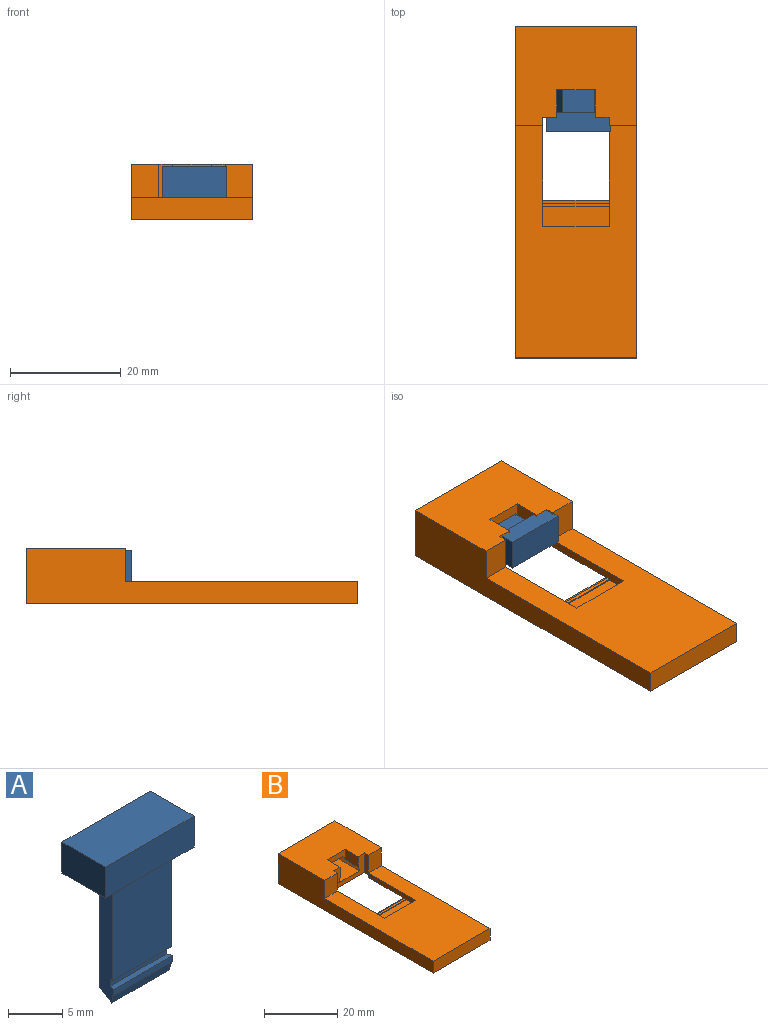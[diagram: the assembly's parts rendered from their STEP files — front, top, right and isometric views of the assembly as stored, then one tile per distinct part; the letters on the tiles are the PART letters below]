
ASSEMBLY  parts=2 mates=1
PART A: 17 faces, bbox 11.6x5.7x17 mm
  f0: plane 13.5x2.8mm, normal (-0.94,0.35,0), area 38.4mm2, adj f2,f3,f4,f5,f6,f7,f8,f9
  f1: plane 13.5x2.8mm, normal (0.94,0.35,0), area 38.4mm2, adj f2,f3,f4,f5,f6,f7,f8,f9
  f2: plane 13.5x5.7mm, normal (0,1,0), area 76.9mm2, adj f0,f1,f4,f9
  f3: plane 10.8x7.7mm, normal (0,-1,0), area 83.2mm2, adj f0,f1,f8,f9
  f4: plane 7.55x2.5mm, normal (0,0,-1), area 16.6mm2, adj f0,f1,f2,f5
  f5: plane 7.7x1mm, normal (0,-0.98,-0.2), area 7.8mm2, adj f0,f1,f4,f16
  f6: plane 7.77x0.6mm, normal (0,0,1), area 4.5mm2, adj f0,f1,f7,f15
  f7: plane 7.33x0.5mm, normal (0,-1,0), area 3.7mm2, adj f0,f1,f6,f8
  f8: cylinder r=0.5mm len=7.7mm, axis (1,0,0), area 5.9mm2, adj f0,f1,f3,f7
  f9: plane 11.6x5.7mm, normal (0,0,-1), area 48mm2, adj f0,f1,f2,f3,f10,f11,f12,f13
  f10: plane 11.6x3.5mm, normal (0,1,0), area 40.6mm2, adj f9,f11,f13,f14
  f11: plane 5.7x3.5mm, normal (-1,0,0), area 19.9mm2, adj f9,f10,f12,f14
  f12: plane 11.6x3.5mm, normal (0,-1,0), area 40.6mm2, adj f9,f11,f13,f14
  f13: plane 5.7x3.5mm, normal (1,0,0), area 19.9mm2, adj f9,f10,f12,f14
  f14: plane 11.6x5.7mm, normal (0,0,1), area 66.1mm2, adj f10,f11,f12,f13
  f15: plane 7.77x0.7mm, normal (0,-1,0), area 5.4mm2, adj f0,f1,f6,f16
  f16: plane 7.77x0.1mm, normal (0,0,-1), area 0.8mm2, adj f0,f1,f5,f15
PART B: 51 faces, bbox 22x60x10 mm
  f0: plane 8x2mm, normal (0,0,1), area 16mm2, adj f3,f43,f44,f48
  f1: plane 22x18mm, normal (0,0,1), area 343mm2, adj f4,f5,f10,f18,f19,f21,f25,f26
  f2: plane 10x6mm, normal (0,0,-1), area 60mm2, adj f3,f43,f44,f47
  f3: plane 15x3mm, normal (0.95,0,-0.32), area 39.5mm2, adj f0,f2,f4,f42,f44,f45,f47,f48
  f4: plane 12x6.5mm, normal (0,-1,0), area 42.2mm2, adj f1,f3,f10,f26,f41,f42,f43,f45
  f5: plane 6x5mm, normal (0,-1,0), area 30mm2, adj f1,f8,f10,f19
  f6: plane 13.5x3.5mm, normal (0,0,-1), area 47.2mm2, adj f10,f11,f15,f39
  f7: plane 13.5x3.5mm, normal (0,0,-1), area 47.2mm2, adj f11,f24,f26,f40
  f8: plane 42x22mm, normal (0,0,1), area 705.6mm2, adj f5,f10,f19,f20,f21,f25,f26,f34
  f9: plane 12x0.5mm, normal (0,0,1), area 6mm2, adj f10,f11,f26,f37
  f10: plane 19.7x7.6mm, normal (1,0,0), area 37.4mm2, adj f1,f4,f5,f6,f8,f9,f11,f34
  f11: plane 19x0.9mm, normal (0,1,0), area 11.6mm2, adj f6,f7,f9,f10,f12,f15,f24,f26
  f12: plane 5.95x5mm, normal (0,0,-1), area 29.7mm2, adj f11,f13,f15,f31
  f13: plane 19x0.9mm, normal (0,-1,0), area 12.8mm2, adj f12,f14,f15,f24,f30,f31,f32,f33
  f14: plane 19x5.2mm, normal (0,0,-1), area 98.8mm2, adj f13,f15,f24,f28
  f15: plane 57x3.5mm, normal (1,0,0), area 154.3mm2, adj f6,f11,f12,f13,f14,f16,f17,f22
  f16: plane 19x16mm, normal (0,0,-1), area 304mm2, adj f15,f22,f24,f27
  f17: plane 60x22mm, normal (0,0,-1), area 237mm2, adj f15,f18,f19,f20,f21,f22,f23,f24
  f18: plane 22x10mm, normal (0,1,0), area 220mm2, adj f1,f17,f19,f21
  f19: plane 60x10mm, normal (-1,0,0), area 348mm2, adj f1,f5,f8,f17,f18,f20
  f20: plane 22x4mm, normal (0,-1,0), area 88mm2, adj f8,f17,f19,f21
  f21: plane 60x10mm, normal (1,0,0), area 348mm2, adj f1,f8,f17,f18,f20,f25
  f22: plane 19x2.5mm, normal (0,1,0), area 47.5mm2, adj f15,f16,f17,f24
  f23: plane 19x3.5mm, normal (0,-1,0), area 66.5mm2, adj f15,f17,f24,f41
  f24: plane 57x3.5mm, normal (-1,0,0), area 154.3mm2, adj f7,f11,f13,f14,f16,f17,f22,f23
  f25: plane 6x5mm, normal (0,-1,0), area 30mm2, adj f1,f8,f21,f26
  f26: plane 19.7x7.6mm, normal (-1,0,0), area 37.4mm2, adj f1,f4,f7,f8,f9,f11,f25,f34
  f27: plane 19x0.3mm, normal (0,-1,0), area 5.7mm2, adj f15,f16,f24,f29
  f28: plane 19x0.3mm, normal (0,1,0), area 5.7mm2, adj f14,f15,f24,f29
  f29: plane 19x0.8mm, normal (0,0,-1), area 15.2mm2, adj f15,f24,f27,f28
  f30: plane 5.95x5mm, normal (0,0,-1), area 29.7mm2, adj f11,f13,f24,f32
  f31: plane 5x0.6mm, normal (1,0,0), area 3mm2, adj f11,f12,f13,f33
  f32: plane 5x0.6mm, normal (-1,0,0), area 3mm2, adj f11,f13,f30,f33
  f33: plane 7.1x5mm, normal (0,0,-1), area 35.5mm2, adj f11,f13,f31,f32
  f34: plane 12x1.6mm, normal (0,1,0), area 19.2mm2, adj f8,f10,f26,f35
  f35: plane 12x3.6mm, normal (0,0,1), area 43.2mm2, adj f10,f26,f34,f36
  f36: plane 12x0.2mm, normal (0,-1,0), area 2.4mm2, adj f10,f26,f35,f38
  f37: plane 12x0.2mm, normal (0,1,0), area 2.4mm2, adj f9,f10,f26,f38
  f38: plane 12x0.6mm, normal (0,0,1), area 7.2mm2, adj f10,f26,f36,f37
  f39: plane 3.5x1mm, normal (0,1,0), area 3.5mm2, adj f6,f10,f15,f41
  f40: plane 3.5x1mm, normal (0,1,0), area 3.5mm2, adj f7,f24,f26,f41
  f41: plane 19x16.5mm, normal (0,0,-1), area 295.5mm2, adj f4,f10,f15,f23,f24,f26,f39,f40
  f42: plane 12.4x8mm, normal (0,0,1), area 99.2mm2, adj f3,f4,f43,f49
  f43: plane 15x3mm, normal (-0.95,0,-0.32), area 39.5mm2, adj f0,f2,f4,f42,f44,f46,f47,f48
  f44: plane 8x3mm, normal (0,-1,0), area 21mm2, adj f0,f2,f3,f43
  f45: plane 5x3.5mm, normal (1,0,0), area 17.5mm2, adj f1,f3,f4,f47
  f46: plane 5x3.5mm, normal (-1,0,0), area 17.5mm2, adj f1,f4,f43,f47
  f47: plane 7x3.5mm, normal (0,-1,0), area 14.8mm2, adj f1,f2,f3,f43,f45,f46
  f48: plane 8x0.1mm, normal (0,1,0), area 0.8mm2, adj f0,f3,f43,f50
  f49: plane 8x0.1mm, normal (0,-1,0), area 0.8mm2, adj f3,f42,f43,f50
  f50: plane 7.93x0.6mm, normal (0,0,1), area 4.8mm2, adj f3,f43,f48,f49
PLACE A rot(axis=(1,0,0),90deg) t=(-0.19,6.48,4.19)mm
PLACE B t=(-0.66,-6.38,-3.51)mm
MATE planar A.f3 <-> B.f42  axis (0,0,-1) through (-0.19,13.38,1.49)mm
